# Revit family: Hitachi_Remote-Controller-PC-ARFG-E_LOD400
name_source: partatom
category: Equipement de génie climatique
revit_build: Autodesk Revit 2018 (Build: 20181015_0930(x64)
units: mm (PartAtom-declared; Revit-internal decimal feet)

## family parameters
Basée sur le plan de construction = Oui
Classification = Aucun
Cote de connecteur circulaire = Utiliser le diamètre
Couper avec des vides une fois chargée = Non
Numéro OmniClass = 23.75.65.14.17
Partagée = Non
Point de calcul de pièce = Non
Titre OmniClass = Control and Monitoring Boards/Panels
Toujours verticalement = Oui
Type d'élément = Normal

## types (1)
- PC-ARFG-E
    BC_OBJECT_ID = 239936
    BC_OBJECT_VERSION = #2
    BC_VARIANT_ID = 616885
    Box = PC-ARFG-E-box
    Color = White
    Commentaires du type = PC-ARFG-E - Advanced color wired remote controller
    Communication Type = HLINK
    Description = Remote Controller PC-ARFG-E
    ETIM Code = EC011603
    Electric Power = 0 W
    Elévation par défaut = 1219 mm
    Fabricant = Hitachi Air Conditioning Europe SAS
    Face = PC-ARFG-E-face
    Frequency = 0 Hz
    IP Protection = 0X
    Manufacturer Product Link = https://documentation.hitachiaircon.com
    Mass = 0.17 kg
    MasterFormat = Electric and Electronic Control System for HVAC
    Masterformat Code = 23 09 33
    Maximum Operating Temperature = 40 °C
    Minimum Operating Temperature = 5 °C
    Modèle = Remote Controller PC-ARFG-E
    Name = Remote Controller PC-ARFG-E
    Name BIM&CO = Panneau de contrôle
    Name ETIM = Accessoires pour climatiseur
    Nominal Current = 0 A
    Nominal Voltage = 5 V
    OMNICLASS Table 23 Code  = 23-27 15 23 11
    Object type = Control Panel
    OmniClass code = 23-27 15 23 11
    OmniClass description = HVAC Main Control Panels
    Omniclass = HVAC Main Control Panels
    Operating Humidity Range = 0
    Overall depth = 22 mm
    Overall height = 121 mm  [stored 0.396982 ft]
    Overall width = 120 mm  [stored 0.393701 ft]
    Product Code = 70510005
    Reference = PC-ARFG-E
    Reference description = PC-ARFG-E - Advanced color wired remote controller
    Screen = PC-ARFG-E-screen
    Uniformat = Contrôle électronique
    Uniformat code = D306002

note: [stored X ft] marks values corroborated as IEEE doubles in the binary element streams (Revit-internal decimal feet)

## geometry (parser evidence)
native form markers: Sweep x2
no freeform markers — native parametric forms only
